# Revit family: Magnuson-KrokMagnetic-CoatHooksMagnetic+
name_source: partatom
category: Furniture
units: mm (PartAtom-declared; Revit-internal decimal feet)

## family parameters
Cut with Voids When Loaded = No
Host = Face
Room Calculation Point = No
Shared = No

## types (1)
- KROK-MA
    Assembly Code = E2020200
    Default Elevation = 48"
    Description = Magnetic coat hook with plastic hook. Krok has a weight capacity of 20lbs
    Hook Finish = MAG - Plastic Black
    Keynote = 12500
    Low Emitting Finish = Yes
    Low Emitting Material = Yes
    Manufacturer = Magnuson Group
    Model = KROK-MA
    Percentage of Recycled Content = 0
    Plate Finish = MAG - Textured painted steel
    Product Documentation Link = https://magnusongroup.com
    Revit Model Built By = https://servex-us.com
    Salvage or Reuse = Yes
    Type Comments = Magnetic Coat Hook
    URL = www.magnusongroup.com

## geometry (parser evidence)
native form markers: Sweep x6
no freeform markers — native parametric forms only
